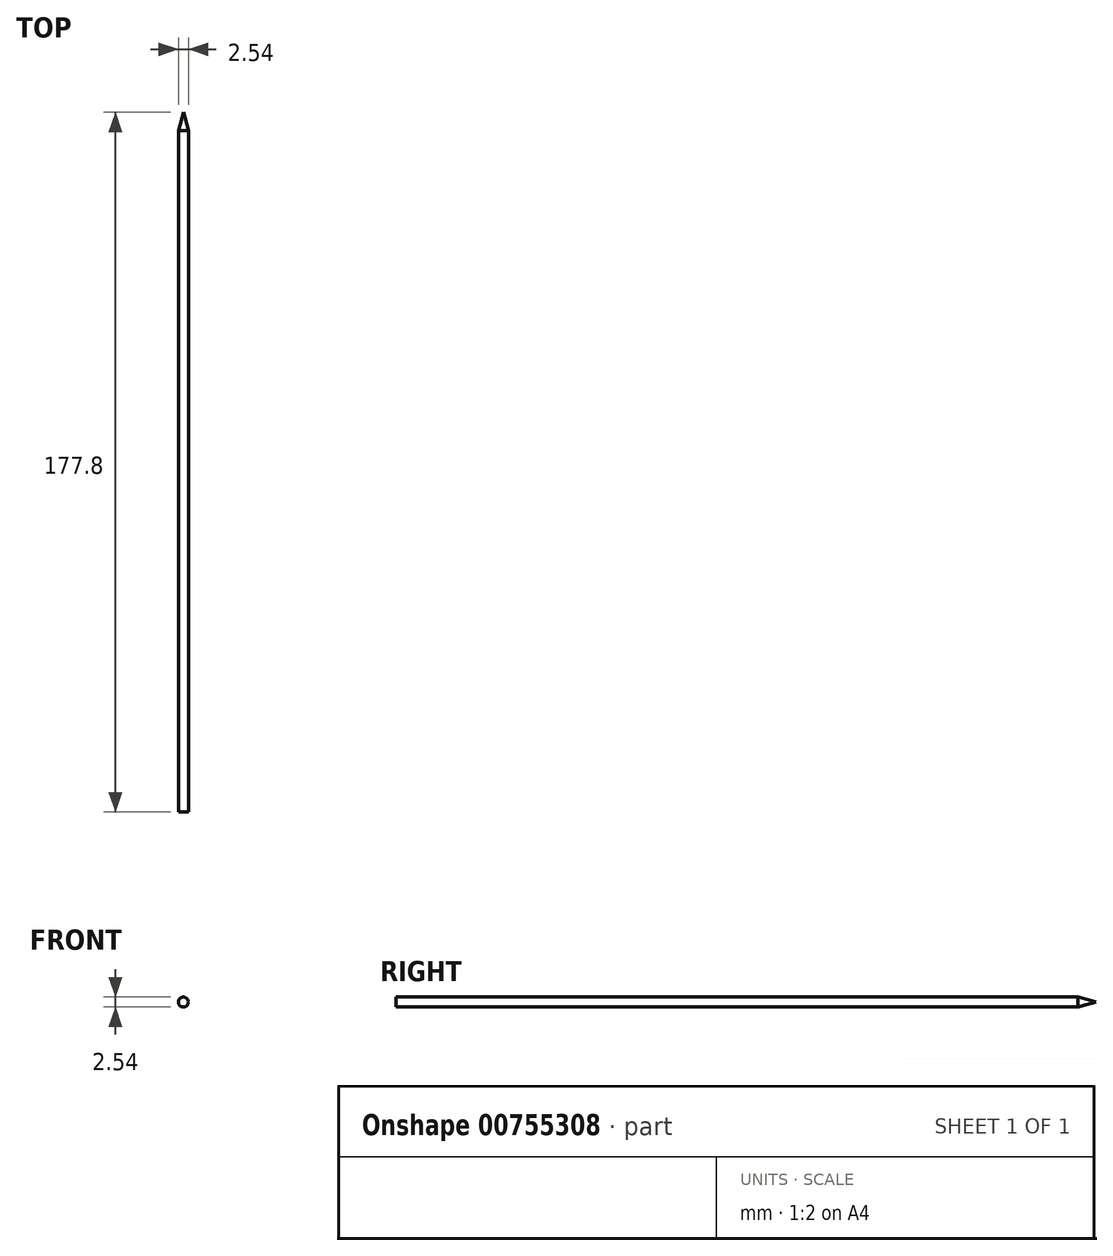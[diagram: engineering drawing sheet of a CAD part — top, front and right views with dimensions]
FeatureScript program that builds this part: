
annotation { "Feature Type Name" : "Feature", "Feature Type Description" : "" }
export const myFeature = defineFeature(function(context is Context, id is Id, definition is map)
    precondition{}
    {
        {
            var Q0;
            Q0=qCreatedBy(makeId("Front.planeOp"),FACE);
            var sketch = newSketch(context, id + "F0", { "sketchPlane" : qUnion([Q0])});
            skCircle(sketch, "E0", {"center": v(0, 0) * mm, "radius": 1.27 * mm});
            skSolve(sketch);
        }
        {
            var Q0;
            Q0=makeQuery(id+"F0.imprint","IMPRINT",FACE,{"disambiguationData":[TD([[makeQuery(id+"F0.imprint","IMPRINT",EDGE,{"derivedFrom":sQuery(id+"F0.wireOp",EDGE,"E0")}),1.0]])]});
            extrude(context, id + "F1", {"entities" : qUnion([Q0]), "depth" : 177.8 * mm, "offsetDistance" : 25.4 * mm, "symmetric" : true});
        }
        {
            var Q0;
            Q0=qCreatedBy(makeId("Top.planeOp"),FACE);
            var sketch = newSketch(context, id + "F2", { "sketchPlane" : qUnion([Q0])});
            skLineSegment(sketch, "E1", {"start": v(0, 88.9) * mm, "end": v(0, 85.04) * mm, "construction": true});
            skLineSegment(sketch, "E2", {"start": v(-1.27, 84.27) * mm, "end": v(-1.27, 93.75) * mm});
            skLineSegment(sketch, "E3", {"start": v(-1.27, 93.75) * mm, "end": v(0, 93.75) * mm});
            skLineSegment(sketch, "E4", {"start": v(0, 93.75) * mm, "end": v(0, 88.9) * mm});
            skLineSegment(sketch, "E5", {"start": v(-1.27, 84.27) * mm, "end": v(0, 88.9) * mm});
            skSolve(sketch);
        }
        {
            var Q0;
            Q0=makeQuery(id+"F2.imprint","IMPRINT",FACE,{"disambiguationData":[TD([[makeQuery(id+"F2.imprint","IMPRINT",EDGE,{"derivedFrom":sQuery(id+"F2.wireOp",EDGE,"E2")}),-1.0]])]});
            var Q1;
            Q1=sQuery(id+"F2.wireOp",EDGE,"E1");
            revolve(context, id + "F3", {"operationType" : NewBodyOperationType.REMOVE, "surfaceOperationType" : NewSurfaceOperationType.NEW, "entities" : qUnion([Q0]), "axis" : qUnion([Q1]), "revolveType" : RevolveType.FULL, "oppositeDirection" : true});
        }
    });
